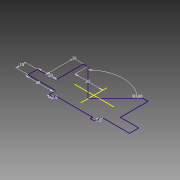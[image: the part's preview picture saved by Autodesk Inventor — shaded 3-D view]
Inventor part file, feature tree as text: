
AUTODESK INVENTOR PART (.ipt)
format: ipt  version: 2015 (Build 190159000, 159)  size: 77,824 bytes
history: native  units: mm
features: sketch x1
ambient origin geometry x8: Origin, YZ Plane, XZ Plane, XY Plane, X Axis, Y Axis, Z Axis, Center Point
feature tree (1):
  sketch  "Sketch1"  dims[d1=90.0deg d3=5.0mm d4=7.5mm d5=30.0mm d6=20.0mm d7=30.0mm d8=2.5mm d9=30.0mm d15=10.0mm]
